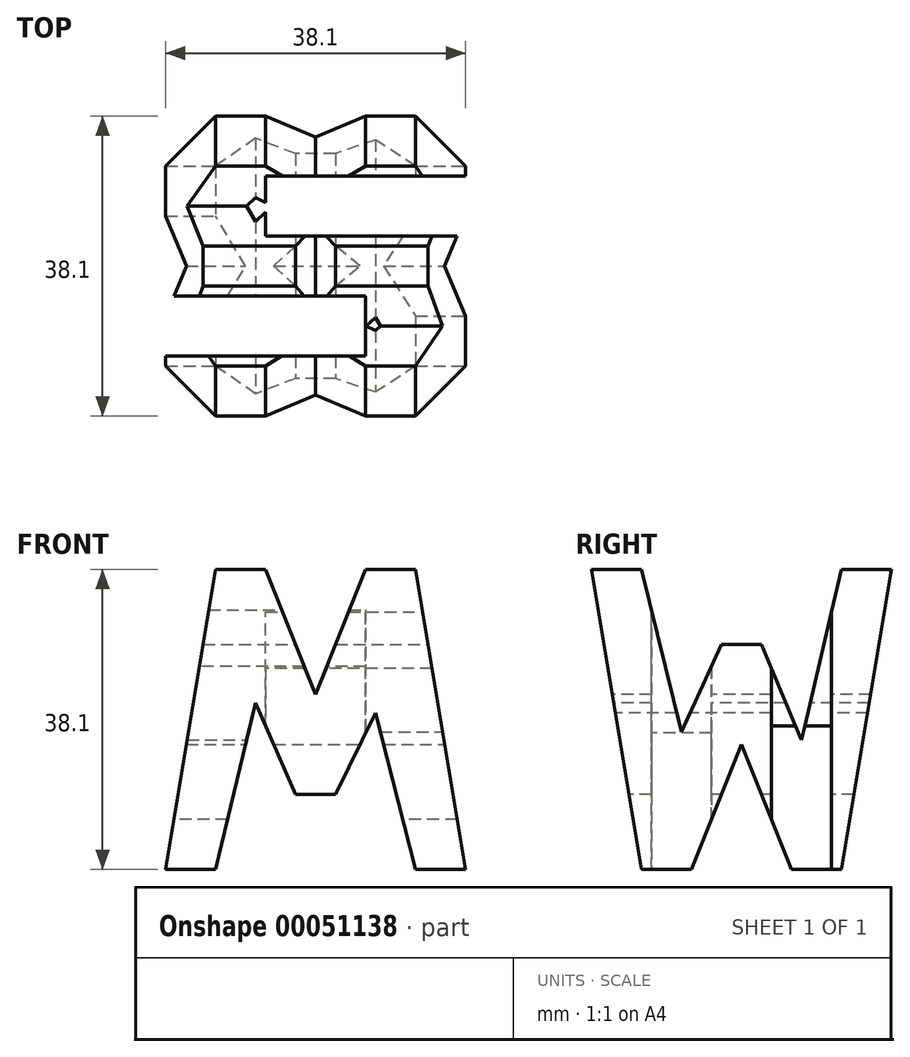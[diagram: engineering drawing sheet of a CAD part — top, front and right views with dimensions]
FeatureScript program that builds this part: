
annotation { "Feature Type Name" : "Feature", "Feature Type Description" : "" }
export const myFeature = defineFeature(function(context is Context, id is Id, definition is map)
    precondition{}
    {
        {
            var Q0;
            Q0=qCreatedBy(makeId("Front.planeOp"),FACE);
            var sketch = newSketch(context, id + "F0", { "sketchPlane" : qUnion([Q0])});
            skLineSegment(sketch, "E0", {"start": v(0, 0) * mm, "end": v(0, 38.1) * mm});
            skLineSegment(sketch, "E1", {"start": v(0, 38.1) * mm, "end": v(-38.1, 38.1) * mm});
            skLineSegment(sketch, "E2", {"start": v(-38.1, 38.1) * mm, "end": v(-38.1, 0) * mm});
            skLineSegment(sketch, "E3", {"start": v(-38.1, 0) * mm, "end": v(0, 0) * mm});
            skSolve(sketch);
        }
        {
            var Q0;
            Q0 = qSketchRegion(id + "F0", true);
            extrude(context, id + "F1", {"entities" : qUnion([Q0]), "depth" : 38.1 * mm});
        }
        {
            var Q0;
            Q0=qCreatedBy(makeId("Front.planeOp"),FACE);
            cPlane(context, id + "F2", {"entities" : qUnion([Q0]), "cplaneType" : CPlaneType.OFFSET, "offset" : 38.1 * mm, "width" : 152.4 * mm, "height" : 152.4 * mm});
        }
        {
            var Q0;
            Q0=qCreatedBy(makeId("Right.planeOp"),FACE);
            cPlane(context, id + "F3", {"entities" : qUnion([Q0]), "cplaneType" : CPlaneType.OFFSET, "offset" : 38.1 * mm, "width" : 152.4 * mm, "height" : 152.4 * mm});
        }
        {
            var Q0;
            Q0=qCreatedBy(makeId("Top.planeOp"),FACE);
            cPlane(context, id + "F4", {"entities" : qUnion([Q0]), "cplaneType" : CPlaneType.OFFSET, "offset" : 38.1 * mm, "width" : 152.4 * mm, "height" : 152.4 * mm});
        }
        {
            var Q0;
            Q0=qCreatedBy(id+"F3.planeOp",FACE);
            var sketch = newSketch(context, id + "F5", { "sketchPlane" : qUnion([Q0])});
            skLineSegment(sketch, "E4.bottom", {"start": v(0, 0) * mm, "end": v(-38.1, 0) * mm});
            skLineSegment(sketch, "E4.top", {"start": v(0, 38.1) * mm, "end": v(-38.1, 38.1) * mm});
            skLineSegment(sketch, "E4.left", {"start": v(0, 0) * mm, "end": v(0, 38.1) * mm});
            skLineSegment(sketch, "E4.right", {"start": v(-38.1, 0) * mm, "end": v(-38.1, 38.1) * mm});
            skLineSegment(sketch, "E5", {"start": v(-38.1, 38.1) * mm, "end": v(-31.75, 0) * mm});
            skLineSegment(sketch, "E6", {"start": v(-25.4, 0) * mm, "end": v(-19.05, 15.87) * mm});
            skLineSegment(sketch, "E7", {"start": v(-19.05, 15.87) * mm, "end": v(-12.7, 0) * mm});
            skLineSegment(sketch, "E8", {"start": v(0, 38.1) * mm, "end": v(-6.35, 0) * mm});
            skLineSegment(sketch, "E9", {"start": v(-31.75, 38.1) * mm, "end": v(-26.67, 17.5) * mm});
            skLineSegment(sketch, "E10", {"start": v(-26.67, 17.5) * mm, "end": v(-21.6, 28.57) * mm});
            skLineSegment(sketch, "E11", {"start": v(-21.6, 28.57) * mm, "end": v(-16.51, 28.57) * mm});
            skLineSegment(sketch, "E12", {"start": v(-16.51, 28.57) * mm, "end": v(-11.43, 16.47) * mm});
            skLineSegment(sketch, "E13", {"start": v(-11.43, 16.47) * mm, "end": v(-6.35, 38.1) * mm});
            skSolve(sketch);
        }
        {
            var Q0;
            {var subQ0=sQuery(id+"F5.wireOp",EDGE,"E9");Q0=makeQuery(id+"F5.imprint","IMPRINT",FACE,{"disambiguationData":[TD([[makeQuery(id+"F5.imprint","IMPRINT",EDGE,{"derivedFrom":subQ0}),1.0]])]});}
            var Q1;
            {var subQ0=sQuery(id+"F5.wireOp",EDGE,"E6");Q1=makeQuery(id+"F5.imprint","IMPRINT",FACE,{"disambiguationData":[TD([[makeQuery(id+"F5.imprint","IMPRINT",EDGE,{"derivedFrom":subQ0}),-1.0]])]});}
            var Q2;
            {var subQ0=sQuery(id+"F5.wireOp",EDGE,"E4.left");Q2=makeQuery(id+"F5.imprint","IMPRINT",FACE,{"disambiguationData":[TD([[makeQuery(id+"F5.imprint","IMPRINT",EDGE,{"derivedFrom":subQ0}),1.0]])]});}
            var Q3;
            {var subQ0=sQuery(id+"F5.wireOp",EDGE,"E4.right");Q3=makeQuery(id+"F5.imprint","IMPRINT",FACE,{"disambiguationData":[TD([[makeQuery(id+"F5.imprint","IMPRINT",EDGE,{"derivedFrom":subQ0}),-1.0]])]});}
            extrude(context, id + "F6", {"entities" : qUnion([Q0, Q1, Q2, Q3]), "operationType" : NewBodyOperationType.REMOVE, "oppositeDirection" : true, "depth" : 76.2 * mm});
        }
        {
            var Q0;
            Q0=qCreatedBy(id+"F2.planeOp",FACE);
            var sketch = newSketch(context, id + "F7", { "sketchPlane" : qUnion([Q0])});
            skLineSegment(sketch, "E14.bottom", {"start": v(0, 0) * mm, "end": v(-38.1, 0) * mm});
            skLineSegment(sketch, "E14.top", {"start": v(0, 38.1) * mm, "end": v(-38.1, 38.1) * mm});
            skLineSegment(sketch, "E14.left", {"start": v(0, 0) * mm, "end": v(0, 38.1) * mm});
            skLineSegment(sketch, "E14.right", {"start": v(-38.1, 0) * mm, "end": v(-38.1, 38.1) * mm});
            skLineSegment(sketch, "E15", {"start": v(-38.1, 0) * mm, "end": v(-31.75, 38.1) * mm});
            skLineSegment(sketch, "E16", {"start": v(-25.4, 38.1) * mm, "end": v(-19.05, 22.22) * mm});
            skLineSegment(sketch, "E17", {"start": v(-19.05, 22.22) * mm, "end": v(-12.7, 38.1) * mm});
            skLineSegment(sketch, "E18", {"start": v(-6.35, 38.1) * mm, "end": v(0, 0) * mm});
            skLineSegment(sketch, "E19", {"start": v(-6.35, 0) * mm, "end": v(-11.43, 19.91) * mm});
            skLineSegment(sketch, "E20", {"start": v(-11.43, 19.91) * mm, "end": v(-16.5, 9.52) * mm});
            skLineSegment(sketch, "E21", {"start": v(-16.5, 9.52) * mm, "end": v(-21.59, 9.52) * mm});
            skLineSegment(sketch, "E22", {"start": v(-21.59, 9.52) * mm, "end": v(-26.67, 21.16) * mm});
            skLineSegment(sketch, "E23", {"start": v(-26.67, 21.16) * mm, "end": v(-31.75, 0) * mm});
            skSolve(sketch);
        }
        {
            var Q0;
            {var subQ0=sQuery(id+"F7.wireOp",EDGE,"E14.right");Q0=makeQuery(id+"F7.imprint","IMPRINT",FACE,{"disambiguationData":[TD([[makeQuery(id+"F7.imprint","IMPRINT",EDGE,{"derivedFrom":subQ0}),-1.0]])]});}
            var Q1;
            {var subQ0=sQuery(id+"F7.wireOp",EDGE,"E16");Q1=makeQuery(id+"F7.imprint","IMPRINT",FACE,{"disambiguationData":[TD([[makeQuery(id+"F7.imprint","IMPRINT",EDGE,{"derivedFrom":subQ0}),1.0]])]});}
            var Q2;
            {var subQ0=sQuery(id+"F7.wireOp",EDGE,"E14.left");Q2=makeQuery(id+"F7.imprint","IMPRINT",FACE,{"disambiguationData":[TD([[makeQuery(id+"F7.imprint","IMPRINT",EDGE,{"derivedFrom":subQ0}),1.0]])]});}
            var Q3;
            {var subQ0=sQuery(id+"F7.wireOp",EDGE,"E19");Q3=makeQuery(id+"F7.imprint","IMPRINT",FACE,{"disambiguationData":[TD([[makeQuery(id+"F7.imprint","IMPRINT",EDGE,{"derivedFrom":subQ0}),1.0]])]});}
            extrude(context, id + "F8", {"entities" : qUnion([Q0, Q1, Q2, Q3]), "operationType" : NewBodyOperationType.REMOVE, "oppositeDirection" : true, "depth" : 38.1 * mm});
        }
        {
            var Q0;
            Q0=qCreatedBy(id+"F4.planeOp",FACE);
            var sketch = newSketch(context, id + "F9", { "sketchPlane" : qUnion([Q0])});
            skLineSegment(sketch, "E24.bottom", {"start": v(0, 0) * mm, "end": v(-38.1, 0) * mm});
            skLineSegment(sketch, "E24.top", {"start": v(0, -38.1) * mm, "end": v(-38.1, -38.1) * mm});
            skLineSegment(sketch, "E24.left", {"start": v(0, 0) * mm, "end": v(0, -38.1) * mm});
            skLineSegment(sketch, "E24.right", {"start": v(-38.1, 0) * mm, "end": v(-38.1, -38.1) * mm});
            skLineSegment(sketch, "E25", {"start": v(0, -7.62) * mm, "end": v(-25.4, -7.62) * mm});
            skLineSegment(sketch, "E26", {"start": v(-25.4, -7.62) * mm, "end": v(-25.4, -15.24) * mm});
            skLineSegment(sketch, "E27", {"start": v(-25.4, -15.24) * mm, "end": v(0, -15.24) * mm});
            skLineSegment(sketch, "E28", {"start": v(-38.1, -22.86) * mm, "end": v(-12.7, -22.86) * mm});
            skLineSegment(sketch, "E29", {"start": v(-12.7, -22.86) * mm, "end": v(-12.7, -30.48) * mm});
            skLineSegment(sketch, "E30", {"start": v(-12.7, -30.48) * mm, "end": v(-38.1, -30.48) * mm});
            skSolve(sketch);
        }
        {
            var Q0;
            {var subQ0=sQuery(id+"F9.wireOp",EDGE,"E25");Q0=makeQuery(id+"F9.imprint","IMPRINT",FACE,{"disambiguationData":[TD([[makeQuery(id+"F9.imprint","IMPRINT",EDGE,{"derivedFrom":subQ0}),1.0]])]});}
            var Q1;
            {var subQ0=sQuery(id+"F9.wireOp",EDGE,"E28");Q1=makeQuery(id+"F9.imprint","IMPRINT",FACE,{"disambiguationData":[TD([[makeQuery(id+"F9.imprint","IMPRINT",EDGE,{"derivedFrom":subQ0}),-1.0]])]});}
            extrude(context, id + "F10", {"entities" : qUnion([Q0, Q1]), "operationType" : NewBodyOperationType.REMOVE, "oppositeDirection" : true, "depth" : 38.1 * mm});
        }
    });
